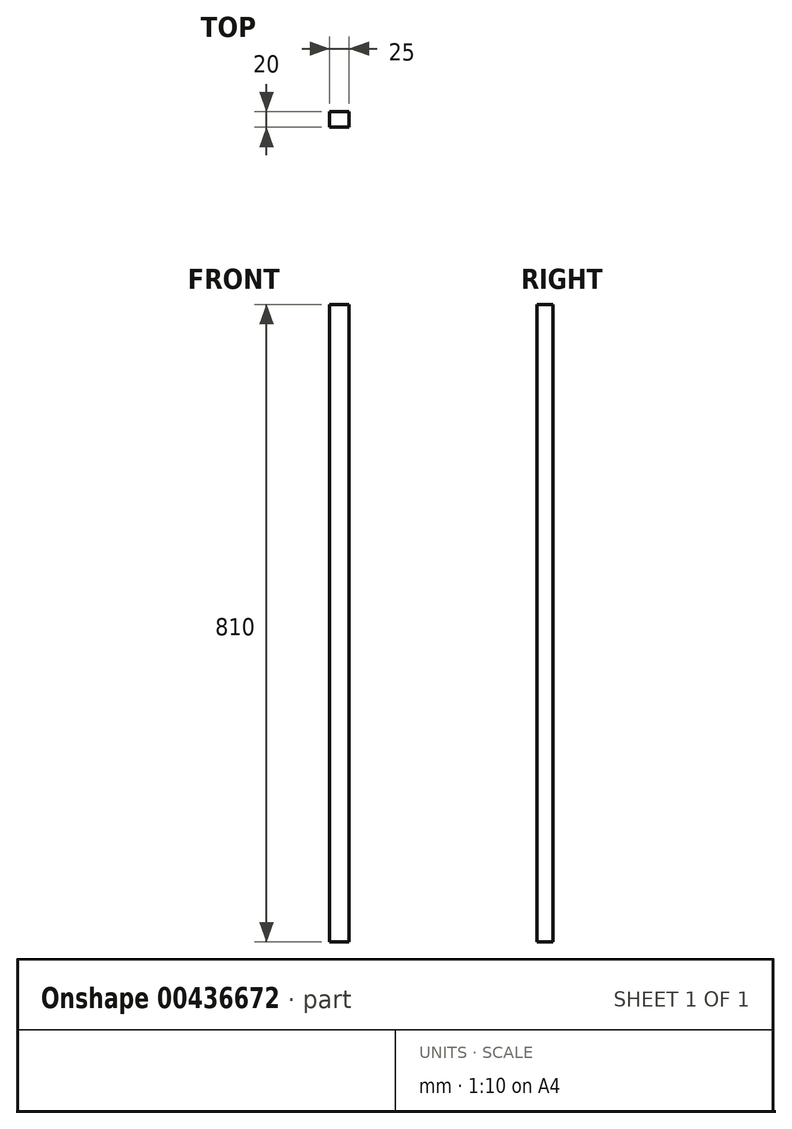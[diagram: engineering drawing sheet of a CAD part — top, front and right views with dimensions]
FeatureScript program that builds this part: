
annotation { "Feature Type Name" : "Feature", "Feature Type Description" : "" }
export const myFeature = defineFeature(function(context is Context, id is Id, definition is map)
    precondition{}
    {
        {
            var Q0;
            Q0=qCreatedBy(makeId("Front.planeOp"),FACE);
            var sketch = newSketch(context, id + "F0", { "sketchPlane" : qUnion([Q0])});
            skLineSegment(sketch, "E0.bottom", {"start": v(12.5, 405) * mm, "end": v(-12.5, 405) * mm});
            skLineSegment(sketch, "E0.top", {"start": v(12.5, -405) * mm, "end": v(-12.5, -405) * mm});
            skLineSegment(sketch, "E0.left", {"start": v(12.5, 405) * mm, "end": v(12.5, -405) * mm});
            skLineSegment(sketch, "E0.right", {"start": v(-12.5, 405) * mm, "end": v(-12.5, -405) * mm});
            skPoint(sketch, "E0.middle", {"position": v(0, 0) * mm});
            skSolve(sketch);
        }
        {
            var Q0;
            Q0 = qSketchRegion(id + "F0", true);
            extrude(context, id + "F1", {"entities" : qUnion([Q0]), "depth" : 20 * mm});
        }
    });
